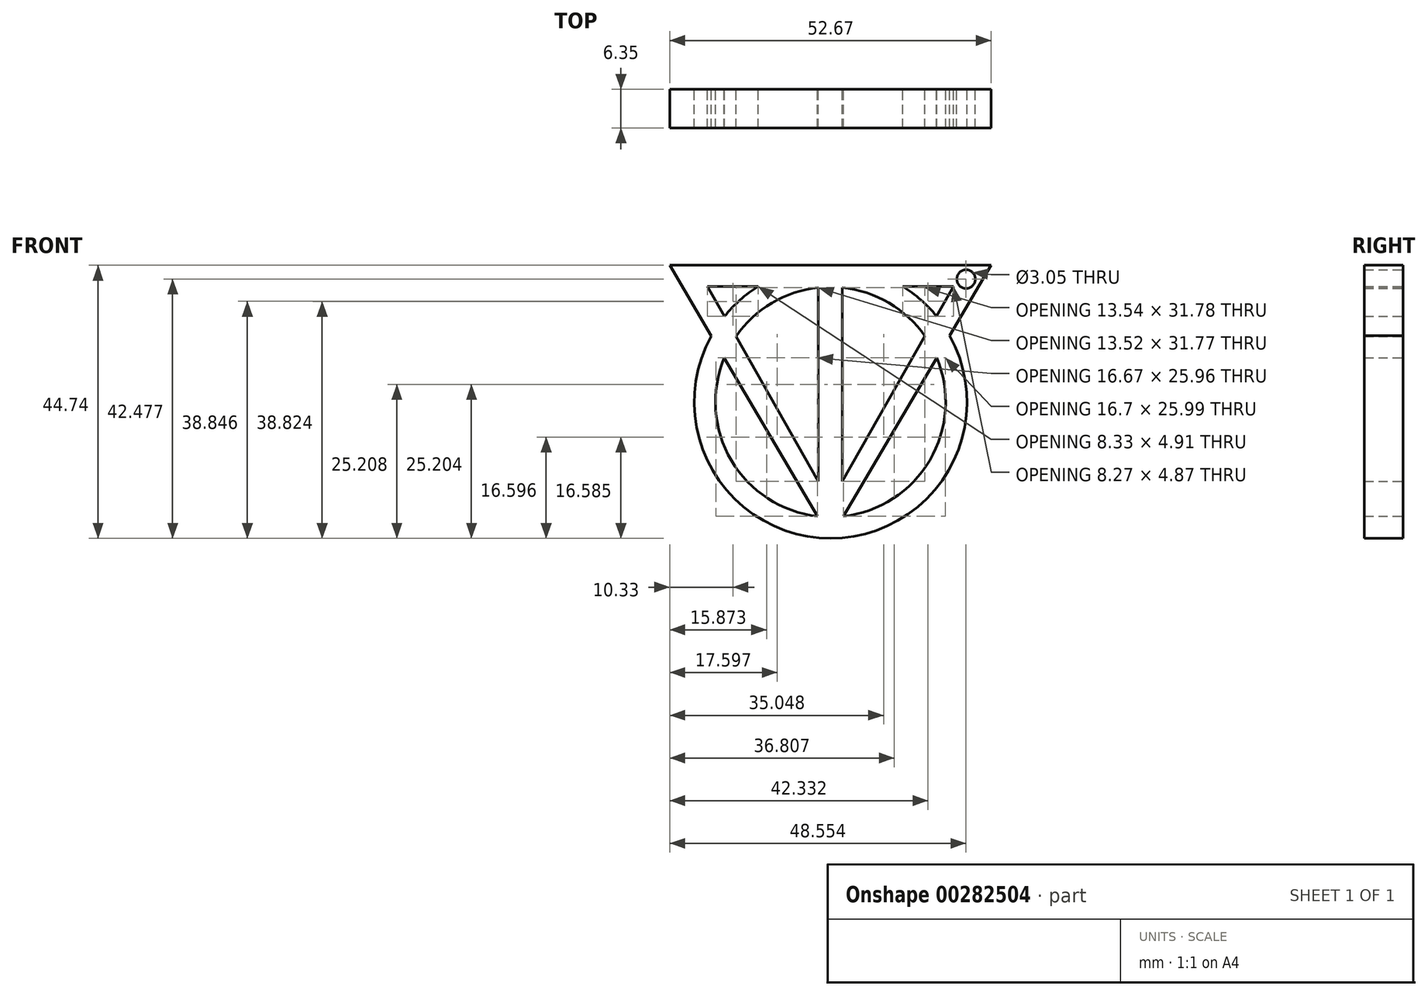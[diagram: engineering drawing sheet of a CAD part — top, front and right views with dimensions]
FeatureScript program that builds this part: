
annotation { "Feature Type Name" : "Feature", "Feature Type Description" : "" }
export const myFeature = defineFeature(function(context is Context, id is Id, definition is map)
    precondition{}
    {
        {
            var Q0;
            Q0=qCreatedBy(makeId("Front.planeOp"),FACE);
            var sketch = newSketch(context, id + "F0", { "sketchPlane" : qUnion([Q0])});
            skLineSegment(sketch, "E0", {"start": v(26.82, 18.56) * mm, "end": v(-25.85, 18.56) * mm});
            skLineSegment(sketch, "E1", {"start": v(26.82, 18.56) * mm, "end": v(0.48, -26.18) * mm});
            skCircle(sketch, "E2", {"center": v(22.7, 16.3) * mm, "radius": 1.52 * mm});
            skLineSegment(sketch, "E3", {"start": v(-25.85, 18.56) * mm, "end": v(0.48, -26.18) * mm});
            skLineSegment(sketch, "E4", {"start": v(20.62, 15.1) * mm, "end": v(-19.69, 15.1) * mm});
            skLineSegment(sketch, "E5", {"start": v(-19.69, 15.1) * mm, "end": v(0.47, -20.3) * mm});
            skLineSegment(sketch, "E6", {"start": v(0.47, -20.3) * mm, "end": v(20.62, 15.1) * mm});
            skCircle(sketch, "E7", {"center": v(0.5, -3.84) * mm, "radius": 22.34 * mm});
            skCircle(sketch, "E8", {"center": v(0.5, -3.84) * mm, "radius": 18.86 * mm});
            skLineSegment(sketch, "E9", {"start": v(-1.5, -16.86) * mm, "end": v(-1.5, 14.9) * mm});
            skLineSegment(sketch, "E10", {"start": v(2.43, -16.86) * mm, "end": v(2.43, 14.92) * mm});
            skSolve(sketch);
        }
        {
            var Q0;
            {var subQ0=sQuery(id+"F0.wireOp",EDGE,"E9");Q0=makeQuery(id+"F0.imprint","IMPRINT",FACE,{"disambiguationData":[TD([[makeQuery(id+"F0.imprint","IMPRINT",EDGE,{"derivedFrom":subQ0}),-1.0]])]});}
            var Q1;
            {var subQ4=sQuery(id+"F0.wireOp",EDGE,"E8");var subQ9=sQuery(id+"F0.wireOp",EDGE,"E1");var subQ10=makeQuery(id+"F0.imprint","INTERSECT",VERTEX,{"disambiguationData":[OD(0.0)],"derivedFrom":[subQ9,subQ4]});Q1=makeQuery(id+"F0.imprint","IMPRINT",FACE,{"disambiguationData":[TD([[makeQuery(id+"F0.imprint","IMPRINT",EDGE,{"disambiguationData":[TD([[subQ10,-1.0]])],"derivedFrom":subQ9}),-1.0]])]});}
            var Q2;
            {var subQ1=sQuery(id+"F0.wireOp",EDGE,"E1");var subQ3=sQuery(id+"F0.wireOp",EDGE,"E8");var subQ4=makeQuery(id+"F0.imprint","INTERSECT",VERTEX,{"disambiguationData":[OD(1.0)],"derivedFrom":[subQ1,subQ3]});Q2=makeQuery(id+"F0.imprint","IMPRINT",FACE,{"disambiguationData":[TD([[makeQuery(id+"F0.imprint","IMPRINT",EDGE,{"disambiguationData":[TD([[subQ4,1.0]])],"derivedFrom":subQ3}),-1.0]])]});}
            var Q3;
            {var subQ0=sQuery(id+"F0.wireOp",EDGE,"E7");var subQ1=sQuery(id+"F0.wireOp",EDGE,"E3");var subQ2=makeQuery(id+"F0.imprint","INTERSECT",VERTEX,{"derivedFrom":[subQ1,subQ0]});Q3=makeQuery(id+"F0.imprint","IMPRINT",FACE,{"disambiguationData":[TD([[makeQuery(id+"F0.imprint","IMPRINT",EDGE,{"disambiguationData":[TD([[subQ2,-1.0]])],"derivedFrom":subQ1}),1.0]])]});}
            var Q4;
            {var subQ11=sQuery(id+"F0.wireOp",EDGE,"E0");Q4=makeQuery(id+"F0.imprint","IMPRINT",FACE,{"disambiguationData":[TD([[makeQuery(id+"F0.imprint","IMPRINT",EDGE,{"derivedFrom":subQ11}),1.0]])]});}
            var Q5;
            {var subQ0=sQuery(id+"F0.wireOp",EDGE,"E7");var subQ1=sQuery(id+"F0.wireOp",EDGE,"E1");var subQ2=makeQuery(id+"F0.imprint","INTERSECT",VERTEX,{"derivedFrom":[subQ1,subQ0]});Q5=makeQuery(id+"F0.imprint","IMPRINT",FACE,{"disambiguationData":[TD([[makeQuery(id+"F0.imprint","IMPRINT",EDGE,{"disambiguationData":[TD([[subQ2,-1.0]])],"derivedFrom":subQ1}),-1.0]])]});}
            var Q6;
            {var subQ0=sQuery(id+"F0.wireOp",EDGE,"E7");var subQ1=sQuery(id+"F0.wireOp",EDGE,"E4");var subQ2=makeQuery(id+"F0.imprint","INTERSECT",VERTEX,{"disambiguationData":[OD(0.0)],"derivedFrom":[subQ1,subQ0]});Q6=makeQuery(id+"F0.imprint","IMPRINT",FACE,{"disambiguationData":[TD([[makeQuery(id+"F0.imprint","IMPRINT",EDGE,{"disambiguationData":[TD([[subQ2,-1.0]])],"derivedFrom":subQ1}),-1.0]])]});}
            var Q7;
            {var subQ0=sQuery(id+"F0.wireOp",EDGE,"E7");var subQ1=sQuery(id+"F0.wireOp",EDGE,"E4");var subQ2=makeQuery(id+"F0.imprint","INTERSECT",VERTEX,{"disambiguationData":[OD(0.0)],"derivedFrom":[subQ1,subQ0]});Q7=makeQuery(id+"F0.imprint","IMPRINT",FACE,{"disambiguationData":[TD([[makeQuery(id+"F0.imprint","IMPRINT",EDGE,{"disambiguationData":[TD([[subQ2,-1.0]])],"derivedFrom":subQ1}),1.0]])]});}
            var Q8;
            {var subQ0=sQuery(id+"F0.wireOp",EDGE,"E7");var subQ1=sQuery(id+"F0.wireOp",EDGE,"E3");var subQ2=makeQuery(id+"F0.imprint","INTERSECT",VERTEX,{"derivedFrom":[subQ1,subQ0]});Q8=makeQuery(id+"F0.imprint","IMPRINT",FACE,{"disambiguationData":[TD([[makeQuery(id+"F0.imprint","IMPRINT",EDGE,{"disambiguationData":[TD([[subQ2,-1.0]])],"derivedFrom":subQ1}),-1.0]])]});}
            var Q9;
            {var subQ0=sQuery(id+"F0.wireOp",EDGE,"E7");var subQ1=sQuery(id+"F0.wireOp",EDGE,"E1");var subQ2=makeQuery(id+"F0.imprint","INTERSECT",VERTEX,{"derivedFrom":[subQ1,subQ0]});Q9=makeQuery(id+"F0.imprint","IMPRINT",FACE,{"disambiguationData":[TD([[makeQuery(id+"F0.imprint","IMPRINT",EDGE,{"disambiguationData":[TD([[subQ2,-1.0]])],"derivedFrom":subQ1}),1.0]])]});}
            extrude(context, id + "F1", {"entities" : qUnion([Q0, Q1, Q2, Q3, Q4, Q5, Q6, Q7, Q8, Q9]), "depth" : 6.35 * mm});
        }
    });
